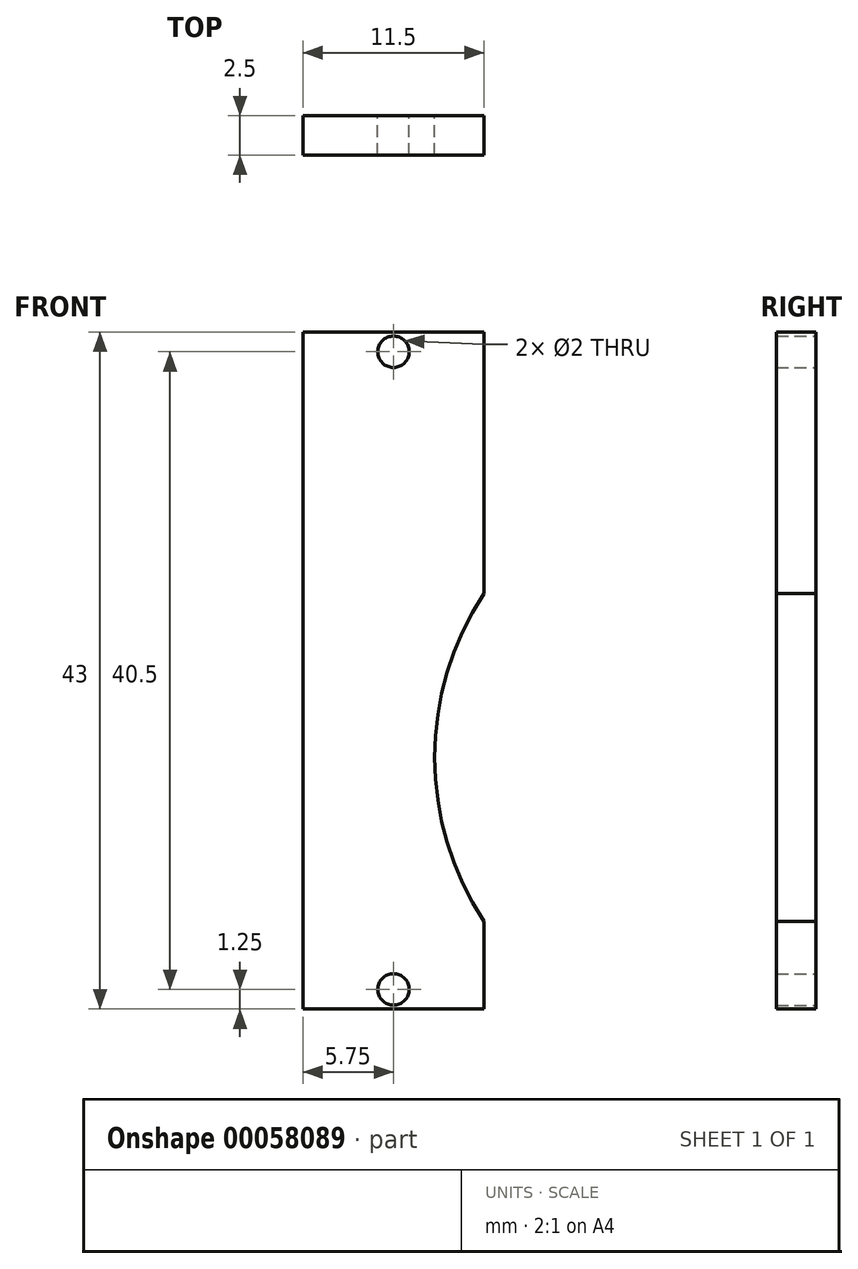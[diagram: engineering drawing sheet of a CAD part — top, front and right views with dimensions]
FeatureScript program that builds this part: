
annotation { "Feature Type Name" : "Feature", "Feature Type Description" : "" }
export const myFeature = defineFeature(function(context is Context, id is Id, definition is map)
    precondition{}
    {
        {
            var Q0;
            Q0=qCreatedBy(makeId("Top.planeOp"),FACE);
            var sketch = newSketch(context, id + "F0", { "sketchPlane" : qUnion([Q0])});
            skLineSegment(sketch, "E0.rect.bottom", {"start": v(5.75, 1.25) * mm, "end": v(-5.75, 1.25) * mm});
            skLineSegment(sketch, "E0.rect.top", {"start": v(5.75, -1.25) * mm, "end": v(-5.75, -1.25) * mm});
            skLineSegment(sketch, "E0.rect.left", {"start": v(5.75, 1.25) * mm, "end": v(5.75, -1.25) * mm});
            skLineSegment(sketch, "E0.rect.right", {"start": v(-5.75, 1.25) * mm, "end": v(-5.75, -1.25) * mm});
            skPoint(sketch, "E0.rect.middle", {"position": v(0, 0) * mm});
            skSolve(sketch);
        }
        {
            var Q0;
            Q0 = qSketchRegion(id + "F0", true);
            var Q1;
            Q1=makeQuery(id+"F0.imprint","IMPRINT",FACE,{"disambiguationData":[TD([[makeQuery(id+"F0.imprint","IMPRINT",EDGE,{"derivedFrom":sQuery(id+"F0.wireOp",EDGE,"E0.rect.bottom")}),1.0]])]});
            extrude(context, id + "F1", {"entities" : qUnion([Q0, Q1]), "depth" : 43 * mm});
        }
        {
            var Q0;
            Q0=makeQuery(id+"F1.opExtrude","SWEPT_FACE",FACE,{"disambiguationData":[OSD([sQuery(id+"F0.wireOp",EDGE,"E0.rect.bottom")])]});
            var sketch = newSketch(context, id + "F2", { "sketchPlane" : qUnion([Q0])});
            skCircle(sketch, "E1", {"center": v(0, 41.75) * mm, "radius": 1 * mm});
            skCircle(sketch, "E2", {"center": v(0, 1.25) * mm, "radius": 1 * mm});
            skPoint(sketch, "E3", {"position": v(0, 43) * mm});
            skSolve(sketch);
        }
        {
            var Q0;
            Q0=makeQuery(id+"F2.imprint","IMPRINT",FACE,{"disambiguationData":[TD([[makeQuery(id+"F2.imprint","IMPRINT",EDGE,{"derivedFrom":sQuery(id+"F2.wireOp",EDGE,"E2")}),1.0]])]});
            var Q1;
            Q1=makeQuery(id+"F2.imprint","IMPRINT",FACE,{"disambiguationData":[TD([[makeQuery(id+"F2.imprint","IMPRINT",EDGE,{"derivedFrom":sQuery(id+"F2.wireOp",EDGE,"E1")}),1.0]])]});
            extrude(context, id + "F3", {"entities" : qUnion([Q0, Q1]), "operationType" : NewBodyOperationType.REMOVE, "oppositeDirection" : true, "depth" : 25 * mm});
        }
        {
            var Q0;
            Q0=makeQuery(id+"F1.opExtrude","SWEPT_FACE",FACE,{"disambiguationData":[OSD([sQuery(id+"F0.wireOp",EDGE,"E0.rect.bottom")])]});
            var sketch = newSketch(context, id + "F4", { "sketchPlane" : qUnion([Q0])});
            skArc(sketch, "E4", {"start": v(-5.75, 5.58) * mm, "mid": v(-2.62, 16) * mm, "end": v(-5.75, 26.4) * mm});
            skSolve(sketch);
        }
        {
            var Q0;
            Q0 = qSketchRegion(id + "F4", true);
            var Q1;
            {var subQ0=sQuery(id+"F4.wireOp",EDGE,"E4");Q1=makeQuery(id+"F4.imprint","IMPRINT",FACE,{"disambiguationData":[TD([[makeQuery(id+"F4.imprint","IMPRINT",EDGE,{"derivedFrom":subQ0}),1.0]])]});}
            extrude(context, id + "F5", {"entities" : qUnion([Q0, Q1]), "operationType" : NewBodyOperationType.REMOVE, "oppositeDirection" : true, "depth" : 25 * mm});
        }
    });
